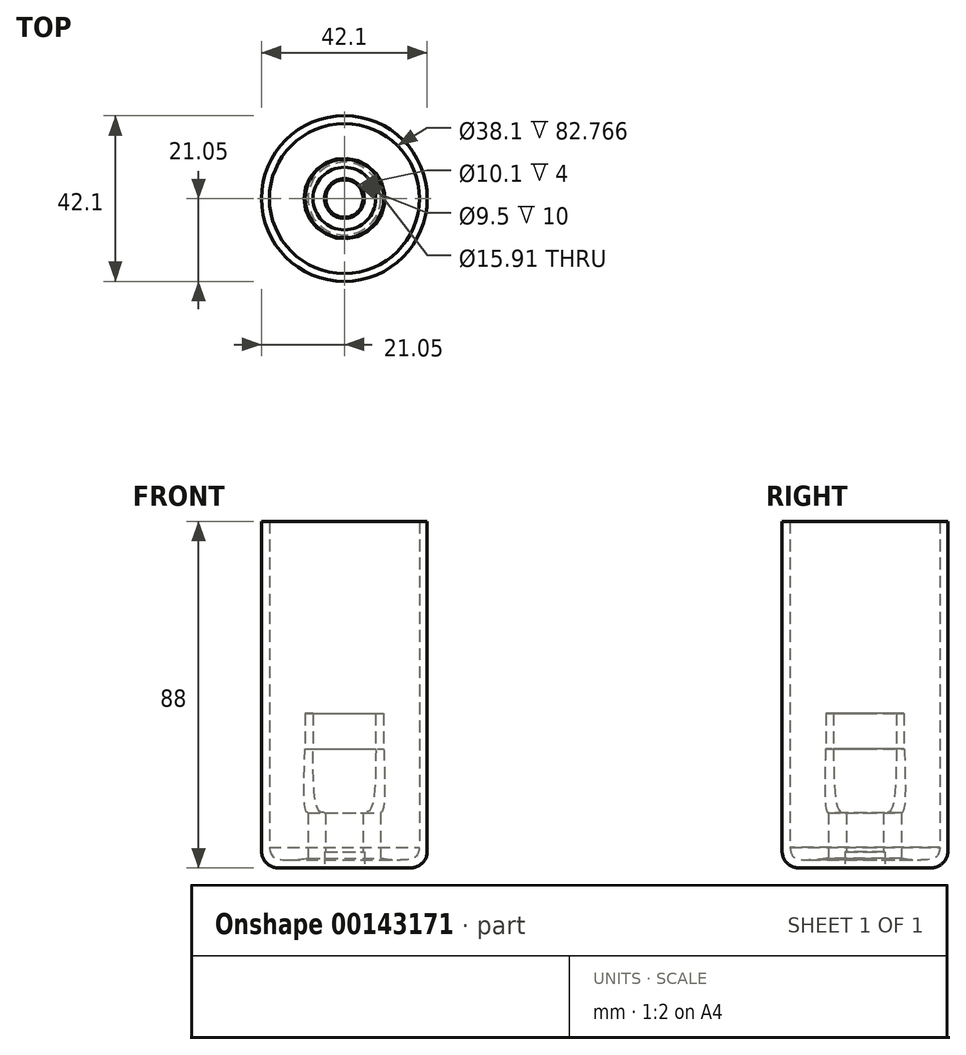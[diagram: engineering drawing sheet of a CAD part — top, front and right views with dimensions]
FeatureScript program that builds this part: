
annotation { "Feature Type Name" : "Feature", "Feature Type Description" : "" }
export const myFeature = defineFeature(function(context is Context, id is Id, definition is map)
    precondition{}
    {
        {
            var Q0;
            Q0=qCreatedBy(makeId("Front.planeOp"),FACE);
            var sketch = newSketch(context, id + "F0", { "sketchPlane" : qUnion([Q0])});
            skLineSegment(sketch, "E0", {"start": v(0, 0) * mm, "end": v(-5.05, 0) * mm});
            skLineSegment(sketch, "E1", {"start": v(-5.05, 0) * mm, "end": v(-21.05, 0) * mm});
            skLineSegment(sketch, "E2", {"start": v(-21.05, 0) * mm, "end": v(-21.05, 88) * mm});
            skLineSegment(sketch, "E3", {"start": v(-5.05, 0) * mm, "end": v(-8.05, 0) * mm});
            skLineSegment(sketch, "E4", {"start": v(-21.05, 88) * mm, "end": v(-19.05, 88) * mm});
            skLineSegment(sketch, "E5", {"start": v(-19.05, 88) * mm, "end": v(-19.05, 5.23) * mm});
            skPoint(sketch, "E6.2.internal.snap0", {"position": v(-13.05, 0) * mm});
            skFitSpline(sketch, "E6", {"points": [v(-19.05, 5.23) * mm, v(-17.97, 2.7) * mm, v(-13.05, 2) * mm, v(-9.23, 2.45) * mm], "startDerivative": vector(1.79, -10.79) * mm, "endDerivative": vector(12.72, 1.96) * mm});
            skLineSegment(sketch, "E7", {"start": v(-5.05, 0) * mm, "end": v(-5.05, 4) * mm});
            skLineSegment(sketch, "E8", {"start": v(-5.05, 4) * mm, "end": v(-4.75, 4) * mm});
            skLineSegment(sketch, "E9", {"start": v(-4.75, 4) * mm, "end": v(-4.75, 14) * mm});
            skLineSegment(sketch, "E10", {"start": v(-4.75, 14) * mm, "end": v(-5.05, 14) * mm});
            skLineSegment(sketch, "E11", {"start": v(-5.05, 14) * mm, "end": v(-9.23, 14) * mm});
            skPoint(sketch, "E12", {"position": v(-9.23, 14) * mm});
            skLineSegment(sketch, "E13", {"start": v(-9.23, 2.45) * mm, "end": v(-9.23, 14) * mm});
            skFitSpline(sketch, "E14", {"points": [v(-9.23, 14) * mm, v(-9.75, 14.44) * mm, v(-10.1, 27.8) * mm, v(-9.95, 30.23) * mm], "startDerivative": vector(-3.51, 0.48) * mm, "endDerivative": vector(0.85, 2.64) * mm});
            skLineSegment(sketch, "E15", {"start": v(-9.95, 30.23) * mm, "end": v(-9.95, 39.23) * mm});
            skLineSegment(sketch, "E16", {"start": v(-7.95, 30.2) * mm, "end": v(-7.95, 39.2) * mm});
            skFitSpline(sketch, "E17", {"points": [v(-5.05, 14) * mm, v(-6.38, 14.43) * mm, v(-7.95, 27.69) * mm, v(-7.95, 30.2) * mm], "startDerivative": vector(-2.56, 1.32) * mm, "endDerivative": vector(0.45, 5.99) * mm});
            skLineSegment(sketch, "E18", {"start": v(-7.95, 39.2) * mm, "end": v(-9.95, 39.23) * mm});
            skLineSegment(sketch, "E19", {"start": v(0, 0) * mm, "end": v(0, 21) * mm});
            skSolve(sketch);
        }
        {
            var Q0;
            Q0=makeQuery(id+"F0.imprint","IMPRINT",FACE,{"disambiguationData":[TD([[makeQuery(id+"F0.imprint","IMPRINT",EDGE,{"derivedFrom":sQuery(id+"F0.wireOp",EDGE,"E11")}),-1.0]])]});
            var Q1;
            Q1=makeQuery(id+"F0.imprint","IMPRINT",FACE,{"disambiguationData":[TD([[makeQuery(id+"F0.imprint","IMPRINT",EDGE,{"derivedFrom":sQuery(id+"F0.wireOp",EDGE,"E1")}),-1.0]])]});
            var Q2;
            Q2=sQuery(id+"F0.wireOp",EDGE,"E19");
            revolve(context, id + "F1", {"entities" : qUnion([Q0, Q1]), "axis" : qUnion([Q2]), "revolveType" : RevolveType.FULL});
        }
        {
            var Q0;
            Q0=makeQuery(id+"F1.opRevolve","SWEPT_EDGE",EDGE,{"disambiguationData":[OSD([sQuery(id+"F0.wireOp",EDGE,"E1"),sQuery(id+"F0.wireOp",EDGE,"E2")])]});
            fillet(context, id + "F2", {"entities" : qUnion([Q0]), "radius" : 4.22 * mm, "tangentPropagation" : true, "allowEdgeOverflow" : false});
        }
    });
